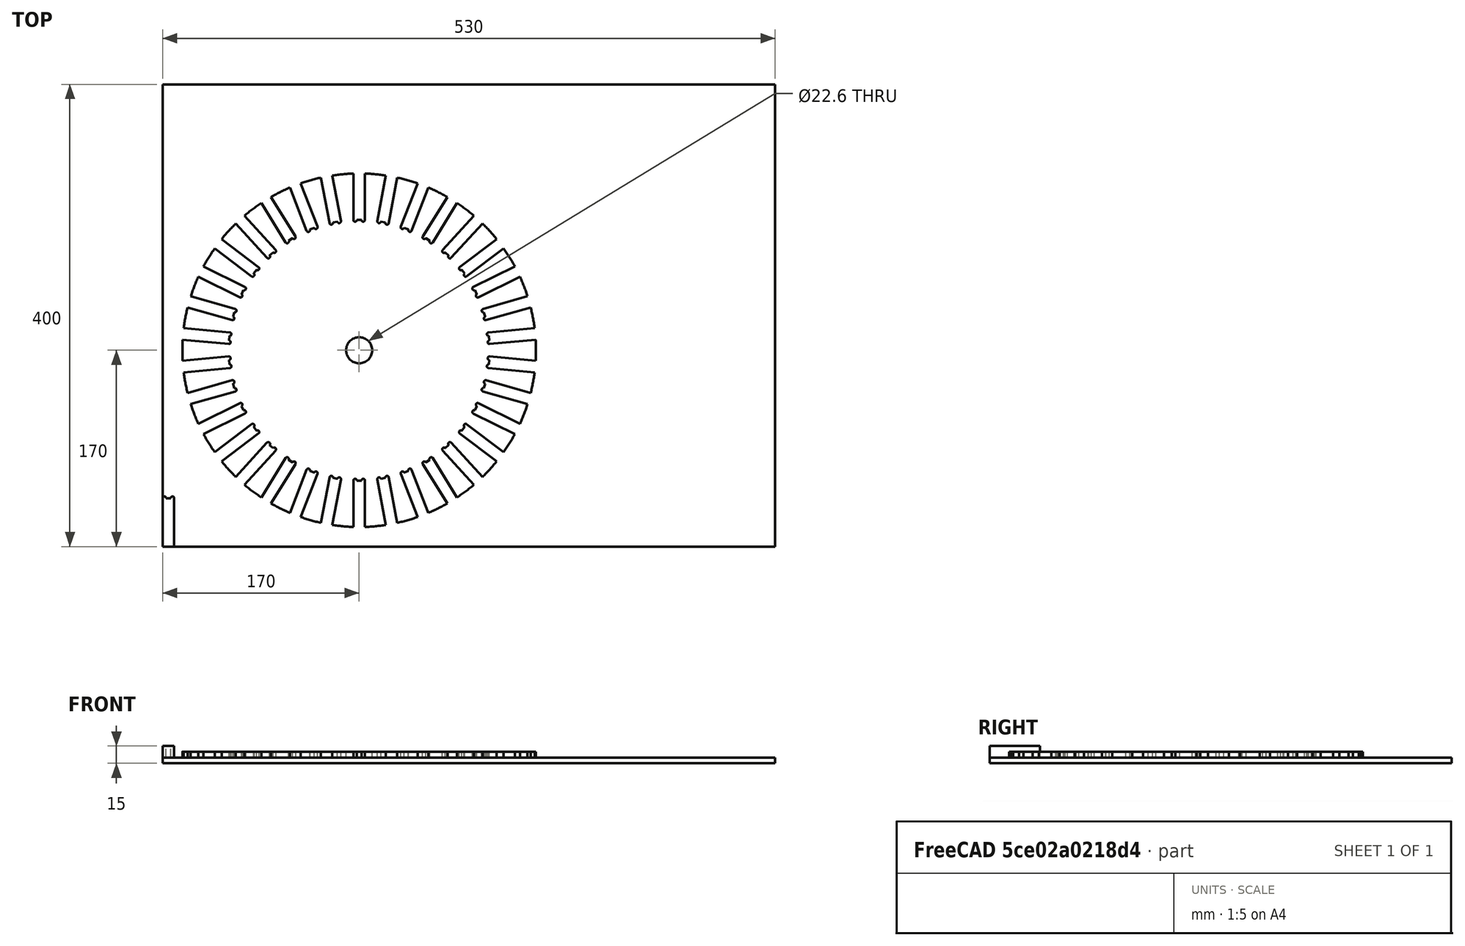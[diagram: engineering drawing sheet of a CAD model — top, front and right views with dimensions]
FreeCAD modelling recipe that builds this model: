
FCSTD DOCUMENT  (FreeCAD 0.17R13327 (Git))
Label: magnetscheibe
License: All rights reserved
LicenseURL: http://en.wikipedia.org/wiki/All_rights_reserved
objects: Part::Cylinder×4, Part::Box×2, Part::Cut×2, Part::MultiFuse×1, Part::Feature×1, Part::FeaturePython×1
note: 11 computed .brp shape members not serialized (recipe doc carries the construction recipe); baked Part::Feature solids carry a one-line shape summary decoded from their .brp

FEATURE [Part::Cylinder] Cylinder  label="Zylinder"
  Angle = 360
  AttacherType = Attacher::AttachEngine3D
  Height = 5
  Radius = 153
FEATURE [Part::Box] Box  label="Würfel"
  AttacherType = Attacher::AttachEngine3D
  Height = 10
  Length = 10
  Width = 42
FEATURE [Part::Cylinder] Cylinder001  label="Zylinder001"
  Angle = 360
  AttacherType = Attacher::AttachEngine3D
  Height = 10
  Placement = pos=(1.5,42,0) rot=(0,0,1;0rad)
  Radius = 1.5
FEATURE [Part::Cylinder] Cylinder002  label="Zylinder002"
  Angle = 360
  AttacherType = Attacher::AttachEngine3D
  Height = 10
  Placement = pos=(8.5,42,0) rot=(0,0,1;0rad)
  Radius = 1.5
FEATURE [Part::MultiFuse] Fusion
  Shapes = -> [Box,Cylinder001,Cylinder002]
FEATURE [Part::Feature] Fusion001
  Placement = pos=(-5,-154.8,0) rot=(0,0,1;0rad)
  shape: bbox 10 x 43.5 x 10 mm, 8 faces (baked)
FEATURE [Part::FeaturePython] Array  # Draft array (typed FeaturePython)
  Angle = 360
  ArrayType = 1
  Axis = (0,0,1)
  Base = -> Fusion001
  Center = (0,0,0)
  Fuse = false
  IntervalAxis = (0,0,0)
  IntervalX = (1,0,0)
  IntervalY = (0,1,0)
  IntervalZ = (0,0,0)
  NumberPolar = 34
  NumberX = 2
  NumberY = 2
  NumberZ = 1
FEATURE [Part::Box] Box001  label="Würfel001"
  AttacherType = Attacher::AttachEngine3D
  Height = 5
  Length = 530
  Placement = pos=(0,0,-5) rot=(0,0,1;0rad)
  Width = 400
FEATURE [Part::Cylinder] Cylinder004  label="Zylinder004"
  Angle = 360
  AttacherType = Attacher::AttachEngine3D
  Height = 5
  Placement = pos=(170,170,0) rot=(0,0,1;0rad)
  Radius = 11.3
FEATURE [Part::Cut] Cut
  Base = -> Cylinder
  Placement = pos=(170,170,0) rot=(0,0,1;0rad)
  Tool = -> Array
FEATURE [Part::Cut] Cut001  label="magnetscheibe"
  Base = -> Cut
  Tool = -> Cylinder004
